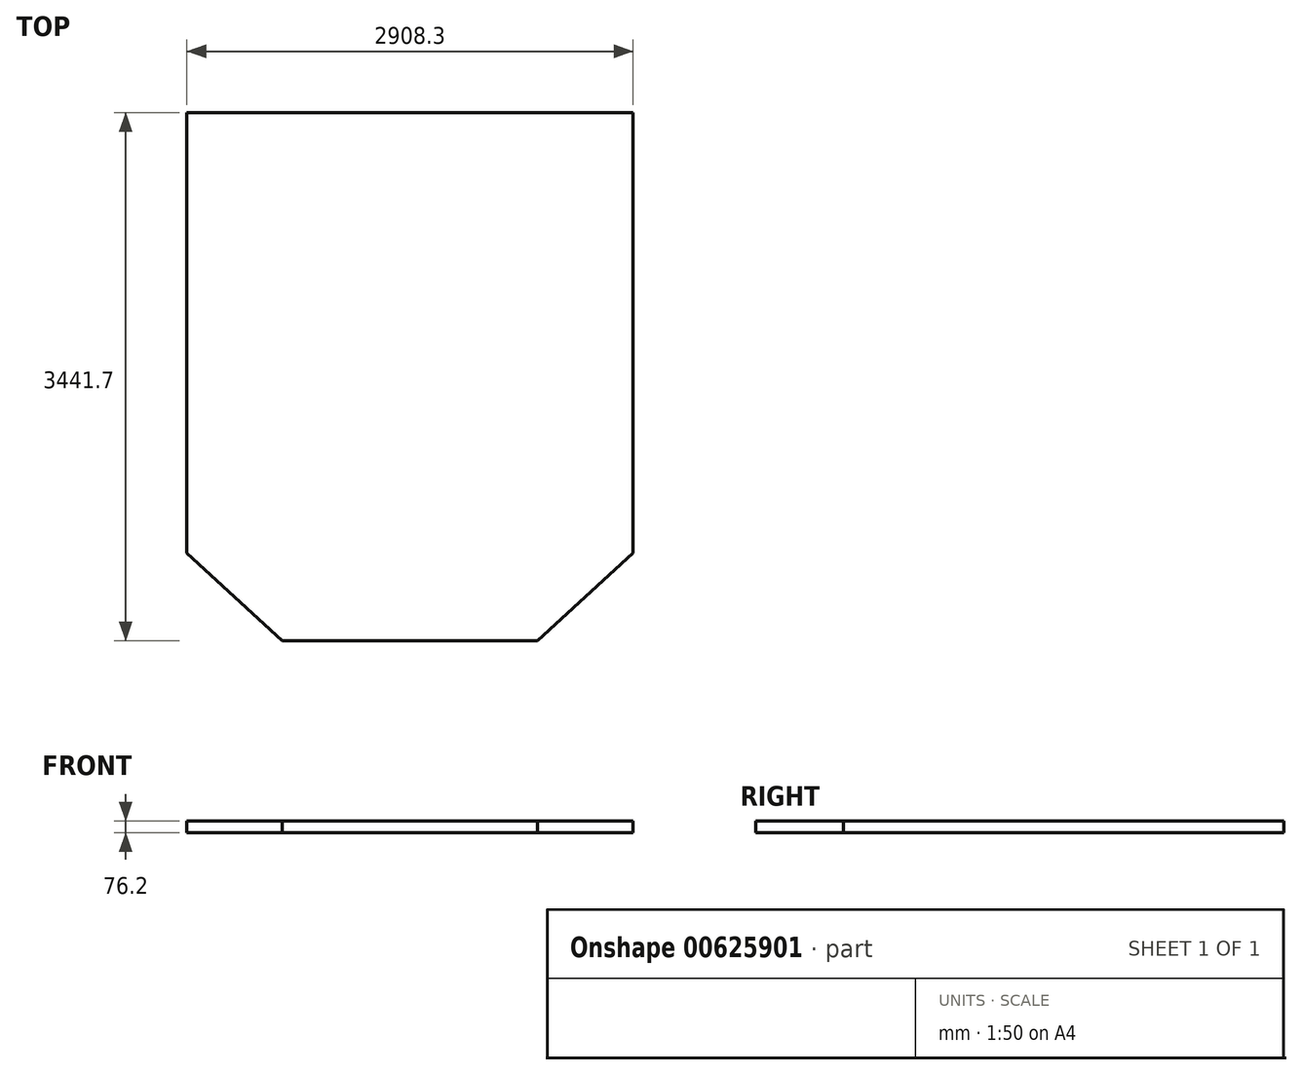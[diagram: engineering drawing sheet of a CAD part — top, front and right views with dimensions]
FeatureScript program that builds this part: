
annotation { "Feature Type Name" : "Feature", "Feature Type Description" : "" }
export const myFeature = defineFeature(function(context is Context, id is Id, definition is map)
    precondition{}
    {
        {
            var Q0;
            Q0=qCreatedBy(makeId("Top.planeOp"),FACE);
            var sketch = newSketch(context, id + "F0", { "sketchPlane" : qUnion([Q0])});
            skLineSegment(sketch, "E0", {"start": v(0, 0) * mm, "end": v(2908.3, 0) * mm});
            skLineSegment(sketch, "E1", {"start": v(2908.3, 0) * mm, "end": v(2908.3, -2870.2) * mm});
            skLineSegment(sketch, "E2", {"start": v(2908.3, -2870.2) * mm, "end": v(2286, -3441.7) * mm});
            skLineSegment(sketch, "E3", {"start": v(2286, -3441.7) * mm, "end": v(622.3, -3441.7) * mm});
            skLineSegment(sketch, "E4", {"start": v(622.3, -3441.7) * mm, "end": v(0, -2870.2) * mm});
            skLineSegment(sketch, "E5", {"start": v(0, -2870.2) * mm, "end": v(0, 0) * mm});
            skSolve(sketch);
        }
        {
            var Q0;
            Q0=makeQuery(id+"F0.imprint","IMPRINT",FACE,{"disambiguationData":[TD([[makeQuery(id+"F0.imprint","IMPRINT",EDGE,{"derivedFrom":sQuery(id+"F0.wireOp",EDGE,"E0")}),-1.0]])]});
            extrude(context, id + "F1", {"entities" : qUnion([Q0]), "oppositeDirection" : true, "depth" : 76.2 * mm, "offsetDistance" : 25.4 * mm});
        }
    });
